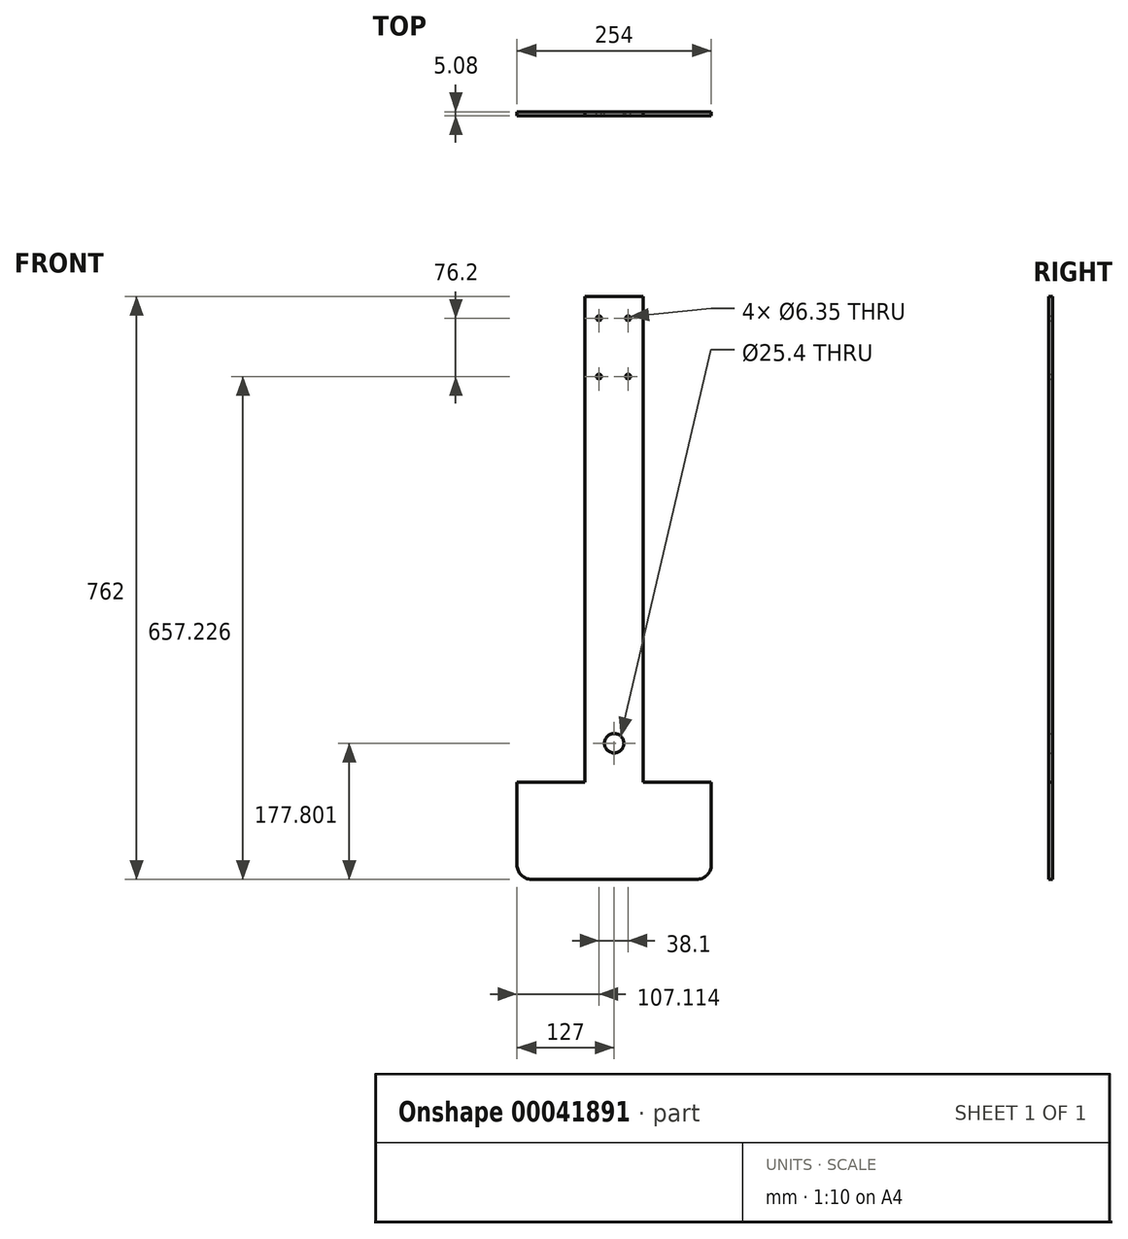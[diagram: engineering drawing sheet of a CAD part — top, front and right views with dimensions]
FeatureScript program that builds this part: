
annotation { "Feature Type Name" : "Feature", "Feature Type Description" : "" }
export const myFeature = defineFeature(function(context is Context, id is Id, definition is map)
    precondition{}
    {
        {
            var Q0;
            Q0=qCreatedBy(makeId("Front.planeOp"),FACE);
            var sketch = newSketch(context, id + "F0", { "sketchPlane" : qUnion([Q0])});
            skLineSegment(sketch, "E0.bottom", {"start": v(-165.1, 61.01) * mm, "end": v(-88.9, 61.01) * mm});
            skLineSegment(sketch, "E0.left", {"start": v(-165.1, 61.01) * mm, "end": v(-165.1, -573.99) * mm});
            skLineSegment(sketch, "E0.right", {"start": v(-88.9, 61.01) * mm, "end": v(-88.9, -573.99) * mm});
            skLineSegment(sketch, "E1.bottom", {"start": v(-254, -573.99) * mm, "end": v(-165.1, -573.99) * mm});
            skLineSegment(sketch, "E1.top", {"start": v(-234.95, -700.99) * mm, "end": v(-19.05, -700.99) * mm});
            skLineSegment(sketch, "E1.left", {"start": v(-254, -573.99) * mm, "end": v(-254, -681.94) * mm});
            skLineSegment(sketch, "E1.right", {"start": v(0, -573.99) * mm, "end": v(0, -681.94) * mm});
            skLineSegment(sketch, "E2.trimOffspring", {"start": v(-88.9, -573.99) * mm, "end": v(0, -573.99) * mm});
            skCircle(sketch, "E3", {"center": v(-127, -523.19) * mm, "radius": 12.7 * mm});
            skCircle(sketch, "E4", {"center": v(-146.89, 32.44) * mm, "radius": 3.18 * mm});
            skCircle(sketch, "E5.1.0.0", {"center": v(-108.79, 32.44) * mm, "radius": 3.18 * mm});
            skLineSegment(sketch, "E5.direction1", {"start": v(-146.89, 32.44) * mm, "end": v(-108.79, 32.44) * mm, "construction": true});
            skLineSegment(sketch, "E6", {"start": v(-131.83, -5.66) * mm, "end": v(-108.62, -5.66) * mm, "construction": true});
            skCircle(sketch, "E7.MirrorC", {"center": v(-146.89, -43.76) * mm, "radius": 3.18 * mm});
            skCircle(sketch, "E8.MirrorC", {"center": v(-108.79, -43.76) * mm, "radius": 3.18 * mm});
            skPoint(sketch, "E9.visualSharp", {"position": v(-254, -700.99) * mm});
            skArc(sketch, "E9.filletArc", {"start": v(-254, -681.94) * mm, "mid": v(-248.42, -695.4) * mm, "end": v(-234.95, -700.99) * mm});
            skPoint(sketch, "E10.visualSharp", {"position": v(0, -700.99) * mm});
            skArc(sketch, "E10.filletArc", {"start": v(-19.05, -700.99) * mm, "mid": v(-5.58, -695.4) * mm, "end": v(0, -681.94) * mm});
            skSolve(sketch);
        }
        {
            var Q0;
            Q0 = qSketchRegion(id + "F0", true);
            extrude(context, id + "F1", {"entities" : qUnion([Q0]), "depth" : 5.08 * mm});
        }
    });
